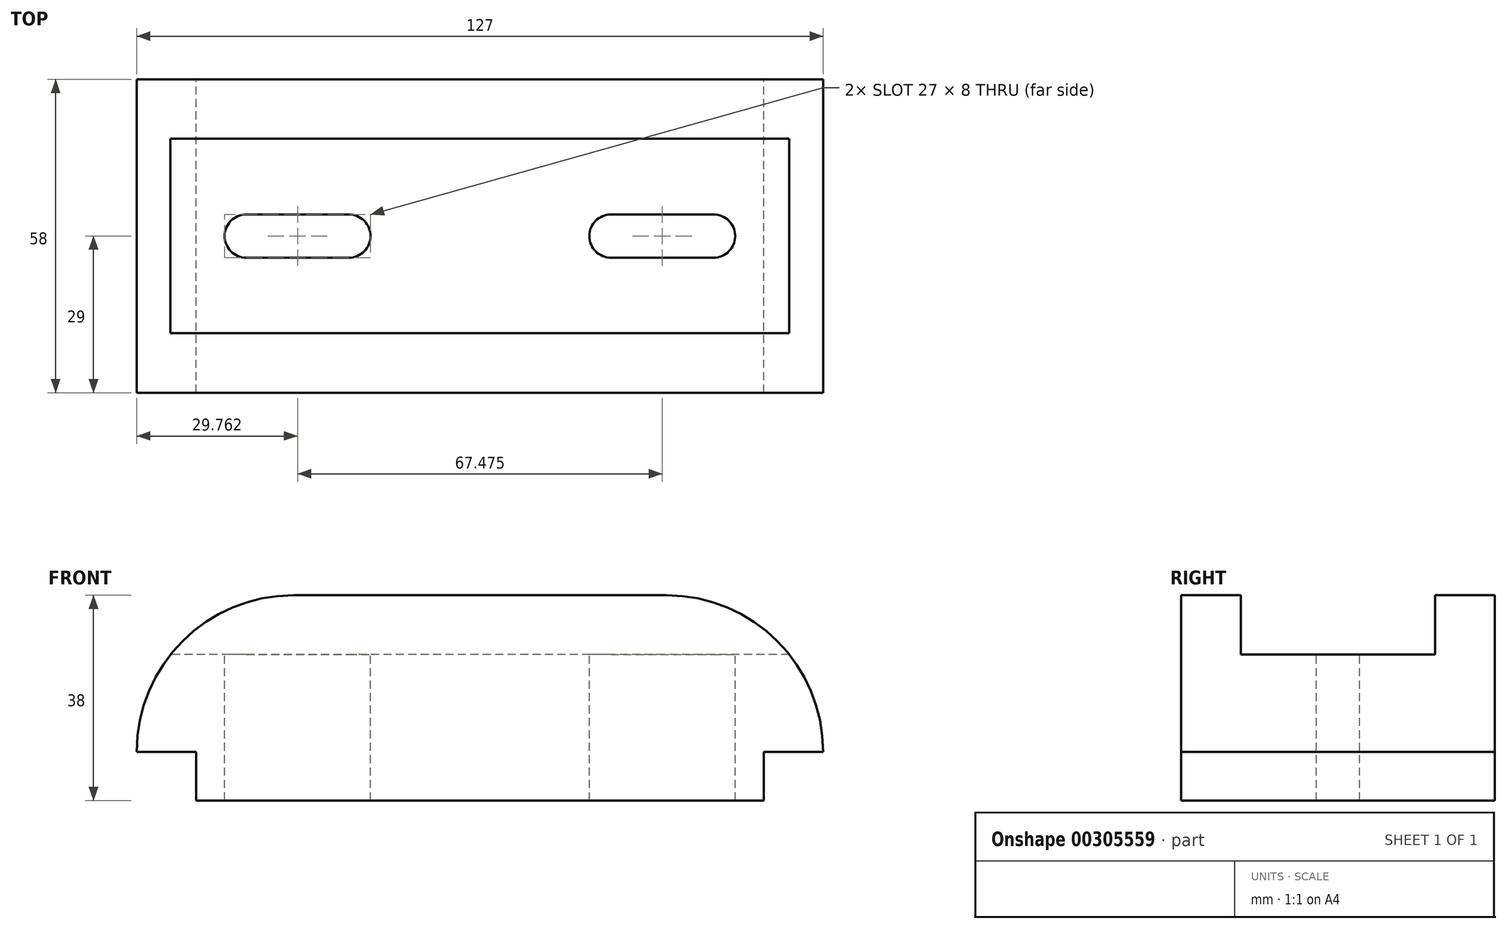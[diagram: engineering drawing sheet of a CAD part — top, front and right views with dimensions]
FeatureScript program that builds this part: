
annotation { "Feature Type Name" : "Feature", "Feature Type Description" : "" }
export const myFeature = defineFeature(function(context is Context, id is Id, definition is map)
    precondition{}
    {
        {
            var Q0;
            Q0=qCreatedBy(makeId("Front.planeOp"),FACE);
            var sketch = newSketch(context, id + "F0", { "sketchPlane" : qUnion([Q0])});
            skLineSegment(sketch, "E0", {"start": v(0, 0) * mm, "end": v(127, 0) * mm});
            skLineSegment(sketch, "E1", {"start": v(127, 0) * mm, "end": v(127, 38) * mm});
            skLineSegment(sketch, "E2", {"start": v(127, 38) * mm, "end": v(0, 38) * mm});
            skLineSegment(sketch, "E3", {"start": v(0, 38) * mm, "end": v(0, 0) * mm});
            skSolve(sketch);
        }
        {
            var Q0;
            Q0 = qSketchRegion(id + "F0", true);
            extrude(context, id + "F1", {"entities" : qUnion([Q0]), "depth" : 58 * mm});
        }
        {
            var Q0;
            Q0=makeQuery(id+"F1.opExtrude","SWEPT_EDGE",EDGE,{"disambiguationData":[OSD([sQuery(id+"F0.wireOp",EDGE,"E2"),sQuery(id+"F0.wireOp",EDGE,"E3")])]});
            var Q1;
            Q1=makeQuery(id+"F1.opExtrude","SWEPT_EDGE",EDGE,{"disambiguationData":[OSD([sQuery(id+"F0.wireOp",EDGE,"E1"),sQuery(id+"F0.wireOp",EDGE,"E2")])]});
            fillet(context, id + "F2", {"entities" : qUnion([Q0, Q1]), "radius" : 29 * mm, "tangentPropagation" : true, "allowEdgeOverflow" : false});
        }
        {
            var Q0;
            Q0=qCreatedBy(makeId("Front.planeOp"),FACE);
            var sketch = newSketch(context, id + "F3", { "sketchPlane" : qUnion([Q0])});
            skLineSegment(sketch, "E4", {"start": v(11, 0) * mm, "end": v(11, 9) * mm});
            skLineSegment(sketch, "E5", {"start": v(11, 9) * mm, "end": v(0, 9) * mm});
            skLineSegment(sketch, "E6", {"start": v(0, 9) * mm, "end": v(0, 0) * mm});
            skLineSegment(sketch, "E7", {"start": v(0, 0) * mm, "end": v(11, 0) * mm});
            skLineSegment(sketch, "E8", {"start": v(127, 0) * mm, "end": v(116, 0) * mm});
            skLineSegment(sketch, "E9", {"start": v(116, 0) * mm, "end": v(116, 9) * mm});
            skLineSegment(sketch, "E10", {"start": v(116, 9) * mm, "end": v(127, 9) * mm});
            skLineSegment(sketch, "E11", {"start": v(127, 9) * mm, "end": v(127, 0) * mm});
            skSolve(sketch);
        }
        {
            var Q0;
            Q0 = qSketchRegion(id + "F3", true);
            extrude(context, id + "F4", {"entities" : qUnion([Q0]), "operationType" : NewBodyOperationType.REMOVE, "endBound" : BoundingType.THROUGH_ALL, "depth" : 25 * mm});
        }
        {
            var Q0;
            Q0=qCreatedBy(makeId("Right.planeOp"),FACE);
            var sketch = newSketch(context, id + "F5", { "sketchPlane" : qUnion([Q0])});
            skLineSegment(sketch, "E12", {"start": v(-47, 38) * mm, "end": v(-47, 27) * mm});
            skLineSegment(sketch, "E13", {"start": v(-47, 27) * mm, "end": v(-11, 27) * mm});
            skLineSegment(sketch, "E14", {"start": v(-11, 27) * mm, "end": v(-11, 38) * mm});
            skLineSegment(sketch, "E15", {"start": v(-11, 38) * mm, "end": v(-47, 38) * mm});
            skSolve(sketch);
        }
        {
            var Q0;
            Q0 = qSketchRegion(id + "F5", true);
            extrude(context, id + "F6", {"entities" : qUnion([Q0]), "operationType" : NewBodyOperationType.REMOVE, "endBound" : BoundingType.THROUGH_ALL, "depth" : 25 * mm});
        }
        {
            var Q0;
            Q0=makeQuery(id+"F6.boolean.opBoolean","COPY",FACE,{"derivedFrom":makeQuery(id+"F6.opExtrude","SWEPT_FACE",FACE,{"disambiguationData":[OSD([sQuery(id+"F5.wireOp",EDGE,"E13")])]})});
            var sketch = newSketch(context, id + "F7", { "sketchPlane" : qUnion([Q0])});
            skLineSegment(sketch, "E16", {"start": v(20.26, -25) * mm, "end": v(39.26, -25) * mm});
            skLineSegment(sketch, "E17", {"start": v(39.26, -33) * mm, "end": v(20.26, -33) * mm});
            skArc(sketch, "E18", {"start": v(20.26, -25) * mm, "mid": v(16.26, -29) * mm, "end": v(20.26, -33) * mm});
            skArc(sketch, "E19", {"start": v(39.26, -33) * mm, "mid": v(43.26, -29) * mm, "end": v(39.26, -25) * mm});
            skLineSegment(sketch, "E20", {"start": v(87.74, -25) * mm, "end": v(106.74, -25) * mm});
            skLineSegment(sketch, "E21", {"start": v(87.74, -33) * mm, "end": v(106.74, -33) * mm});
            skArc(sketch, "E22", {"start": v(87.74, -25) * mm, "mid": v(83.74, -29) * mm, "end": v(87.74, -33) * mm});
            skArc(sketch, "E23", {"start": v(106.74, -33) * mm, "mid": v(110.74, -29) * mm, "end": v(106.74, -25) * mm});
            skSolve(sketch);
        }
        {
            var Q0;
            Q0 = qSketchRegion(id + "F7", true);
            extrude(context, id + "F8", {"entities" : qUnion([Q0]), "operationType" : NewBodyOperationType.REMOVE, "endBound" : BoundingType.THROUGH_ALL, "oppositeDirection" : true, "depth" : 25 * mm});
        }
    });
